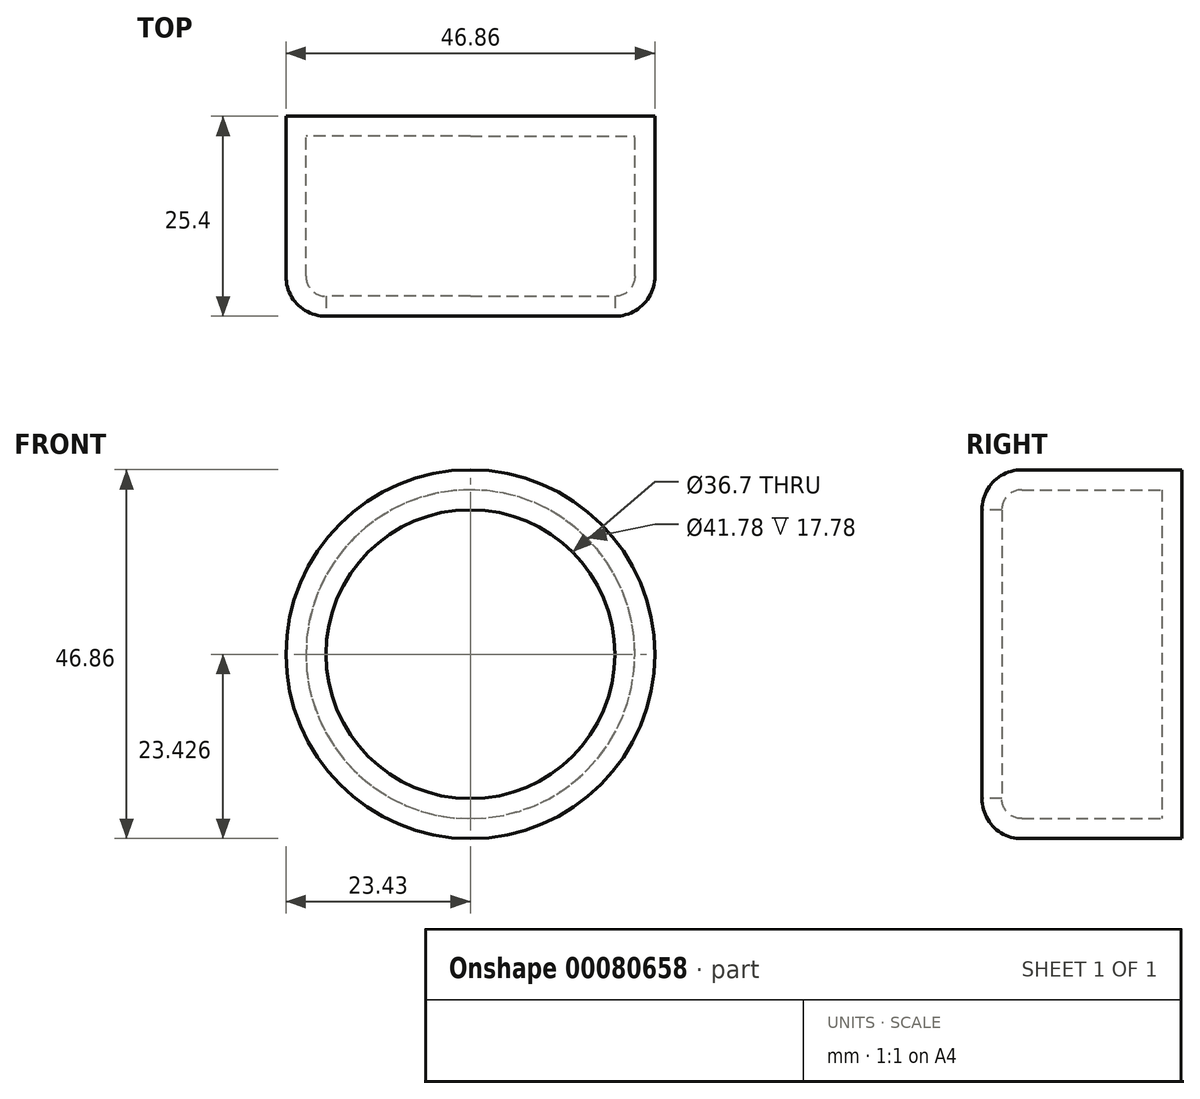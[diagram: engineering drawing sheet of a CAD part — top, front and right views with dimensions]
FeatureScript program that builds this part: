
annotation { "Feature Type Name" : "Feature", "Feature Type Description" : "" }
export const myFeature = defineFeature(function(context is Context, id is Id, definition is map)
    precondition{}
    {
        {
            var Q0;
            Q0=qCreatedBy(makeId("Front.planeOp"),FACE);
            var sketch = newSketch(context, id + "F0", { "sketchPlane" : qUnion([Q0])});
            skCircle(sketch, "E0", {"center": v(0, 0) * mm, "radius": 63.24 * mm});
            skCircle(sketch, "E1", {"center": v(0, 0) * mm, "radius": 39.72 * mm});
            skCircle(sketch, "E2", {"center": v(0, 0) * mm, "radius": 19.88 * mm});
            skSolve(sketch);
        }
        {
            var Q0;
            Q0=sQuery(id+"F0.wireOp",EDGE,"E2");
            extrude(context, id + "F1", {"bodyType" : ToolBodyType.SURFACE, "surfaceEntities" : qUnion([Q0]), "depth" : 25.4 * mm});
        }
        {
            var Q0;
            Q0=qCreatedBy(makeId("Front.planeOp"),FACE);
            var sketch = newSketch(context, id + "F2", { "sketchPlane" : qUnion([Q0])});
            skCircle(sketch, "E3", {"center": v(0, 28.47) * mm, "radius": 23.43 * mm});
            skSolve(sketch);
        }
        {
            var Q0;
            Q0=makeQuery(id+"F2.imprint","IMPRINT",FACE,{"disambiguationData":[TD([[makeQuery(id+"F2.imprint","IMPRINT",EDGE,{"derivedFrom":sQuery(id+"F2.wireOp",EDGE,"E3")}),1.0]])]});
            extrude(context, id + "F3", {"entities" : qUnion([Q0]), "depth" : 25.4 * mm});
        }
        {
            var Q0;
            Q0=makeQuery(id+"F3.opExtrude","CAP_FACE",FACE,{"disambiguationData":[OSD([sQuery(id+"F2.wireOp",EDGE,"E3")])],"isStart":false});
            var Q1;
            Q1=makeQuery(id+"F1.opExtrude","SWEPT_FACE",FACE,{"disambiguationData":[OSD([sQuery(id+"F0.wireOp",EDGE,"E2")])]});
            fillet(context, id + "F4", {"entities" : qUnion([Q0, Q1]), "radius" : 5.08 * mm, "tangentPropagation" : true, "allowEdgeOverflow" : false});
        }
        {
            var Q0;
            Q0=makeQuery(id+"F3.opExtrude","CAP_FACE",FACE,{"disambiguationData":[OSD([sQuery(id+"F2.wireOp",EDGE,"E3")])],"isStart":false});
            shell(context, id + "F5", {"entities" : qUnion([Q0]), "thickness" : 2.54 * mm});
        }
    });
